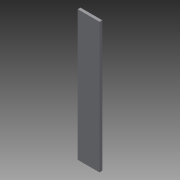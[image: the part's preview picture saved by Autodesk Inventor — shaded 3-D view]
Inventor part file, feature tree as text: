
AUTODESK INVENTOR PART (.ipt)
format: ipt  version: 2016 (Build 200138000, 138)  size: 69,632 bytes
history: native  units: in
note: dims shown in document units (in); Inventor stores cm internally (conversion verified against a paired STEP export)
features: extrude x1, sketch x1
ambient origin geometry x8: Origin, YZ Plane, XZ Plane, XY Plane, X Axis, Y Axis, Z Axis, Center Point
bodies: Solid1 (feature_tree)
feature tree (2):
  extrude  "Extrusion1"  Depth=3.0in
  sketch  "Sketch1"  dims[d0=1.0in d1=3.0in d2=0.125in d3=0.0in]
